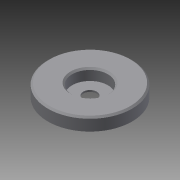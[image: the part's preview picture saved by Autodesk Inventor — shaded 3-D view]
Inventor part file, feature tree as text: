
AUTODESK INVENTOR PART (.ipt)
format: ipt  version: 2014 (Build 180170000, 170)  size: 98,304 bytes
history: native  units: mm
features: extrude x3, sketch x3, chamfer x2
ambient origin geometry x8: Origin, YZ Plane, XZ Plane, XY Plane, X Axis, Y Axis, Z Axis, Center Point
bodies: Solid1 (feature_tree)
feature tree (8):
  extrude  "Extrusion1"  Depth=8.0mm TaperAngle=0.0deg
  extrude  "Extrusion2"  Depth=8.0mm TaperAngle=0.0deg
  extrude  "Extrusion3"  Depth=7.0mm TaperAngle=0.0deg
  chamfer  "Chamfer1"  Distance=1.0mm Angle=45.0deg
  chamfer  "Chamfer2"  Distance=1.0mm Angle=45.0deg
  sketch  "Sketch1"  dims[d0=53.0mm d1=8.0mm d2=0.0mm]
  sketch  "Sketch2"  dims[d3=8.5mm d4=8.0mm d5=0.0mm]
  sketch  "Sketch3"  dims[d6=22.5mm d7=7.0mm d8=0.0mm d9=1.0mm d10=2.0mm d11=45.0deg d12=1.0mm d13=2.0mm d14=45.0deg]
